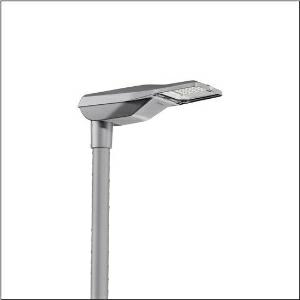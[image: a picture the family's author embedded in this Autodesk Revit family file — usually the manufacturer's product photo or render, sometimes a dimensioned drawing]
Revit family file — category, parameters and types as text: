
# Revit family: streetlight_sl_21_iq_micro___st1_5a_5xe1p41g08cb_60b9
name_source: partatom
category: Lighting Fixtures
units: mm (PartAtom-declared; Revit-internal decimal feet)

## family parameters
Cut with Voids When Loaded = No
Host = Face
Light Source = No
Part Type = Normal
Room Calculation Point = No
Round Connector Dimension = Use Diameter
Shared = No

## types (1)
- --- (1 x LED, 2930 lm, 19.4 W, 4000K)
    Apparent Load = 19 VA
    CIE Flux Codes = 22 53 95 100 100
    Color Rendering = 70
    Color Temperature = 4000K
    Default Elevation = 1800 mm
    Description = Streetlight SL 21 iQ micro, mast luminaire, primary light control with lens, of PMMA, primary optical cover: cover, of toughened safety glass, transparent, light distribution: ST1.5a, light emission: direct distribution, primary light characteristic: asymmetric, installation type: post-top, side-entry, LED, High Power LED, rated luminous flux: 2.930lm, luminous efficacy: 151lm/W, light colour: 740, colour temperature: 4000K, control gear: iQ Street-Remote, control: Street-Remote, Auto-Match, Temp-Guard, Lumen-Switch, Night-Set, Smart-Wire, Light-Fading, Desk-Remote (wireless, voltage-free reading and setting of iQ features in the workshop via application-optimized NFC function/RFID function), optimised constant luminous flux control (CLO 2.0), pre-setting: linear dimming characteristic, mains connection: 220..240V, AC, 50/60Hz, start of lifetime: 19W, end of service life: 20W, reduction: 10W, luminaire housing, of diecast aluminium, powder-coated, SITECO metallic grey (DB 702S), corrosivity category C5 high according to DIN EN ISO 12944, please order mast flange separately, inclination adjustable: 0°, 5°, 10°, 15°, sealing non-destructively replaceable, multi-level sealing system, length: 528mm, width: 235mm, height: 110mm, mast flange for spigot size: 42mm (side-entry): 5XC10008XM4, 60/48mm (side-entry/post-top): 5XC10108XM2, 76/60mm (side-entry/post-top): 5XC10108XM1, protection rating (complete): IP66, insulation class (complete): insulation class II (safety insulation), certification: CE, ENEC, ENEC+, VDE, impact resistance: IK10, permissible operating ambient temperature for outdoor applications: -40..+50°C, standard-compliant lighting for roads and squares, packaging unit: 1 piece

Light Distribution: ST1.5a
    Height = 110 mm
    Lamp = 1 x LED
    Lamp Light Flux = 2930 lm
    Lamp Power = 19.4 W
    Lamp count = 1
    Length = 528 mm
    Luminous efficacy = 151 lm/W
    Manufacturer = Siteco
    ModVariant = No
    Model = 5XE1P41G08CB
    Number of Poles = 1
    OnlyDefault = Yes
    Power Factor = 1
    Product Name = Streetlight SL 21 iQ micro | ST1.5a
    Product group = mast luminaire | pylon top
    ProductGroupID = 6100
    Protection Class = Protection class II
    Protection Degree = IP 66
    RLX_Detail_Level = 1
    RLX_Emergency_Light_Flux = 0 lm
    RLX_Emergency_Type = 0
    RLX_Emergency_Type_DB = No
    RlxData = <blob elided: 103041 chars, md5=1f7dd716>
    Socket = socket
    Standby Power = 0 W
    System Light Flux = 2930 lm
    System Power = 19 W
    Type Comments = factory setting: luminous flux: 100 % | dim-lin: 254 | 387 mA
    Type Image = l_1006881.jpg
    URL = http://relux.com
    VarID = @adj_137495
    Voltage = 0 V
    Weight = 0.00 kg
    Width = 235 mm

## geometry (parser evidence)
native form markers: Blend x4, Sweep x10
no freeform markers — native parametric forms only
